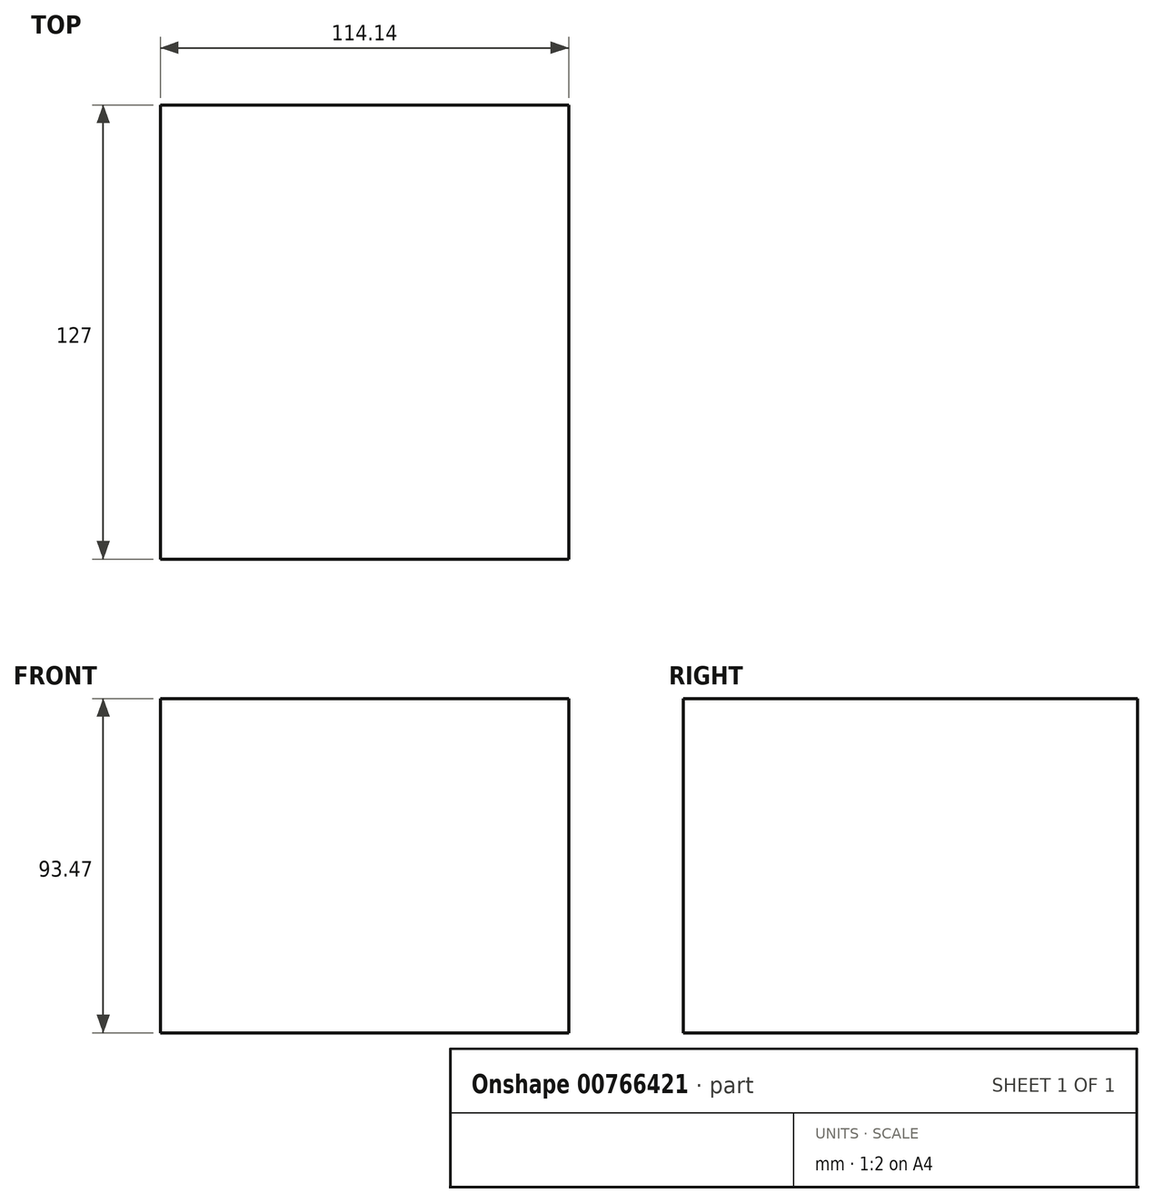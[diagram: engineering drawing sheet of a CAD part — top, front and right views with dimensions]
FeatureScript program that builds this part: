
annotation { "Feature Type Name" : "Feature", "Feature Type Description" : "" }
export const myFeature = defineFeature(function(context is Context, id is Id, definition is map)
    precondition{}
    {
        {
            var Q0;
            Q0=qCreatedBy(makeId("Front.planeOp"),FACE);
            var sketch = newSketch(context, id + "F0", { "sketchPlane" : qUnion([Q0])});
            skLineSegment(sketch, "E0.bottom", {"start": v(-44.65, 36.3) * mm, "end": v(69.49, 36.3) * mm});
            skLineSegment(sketch, "E0.top", {"start": v(-44.65, -57.16) * mm, "end": v(69.49, -57.16) * mm});
            skLineSegment(sketch, "E0.left", {"start": v(-44.65, 36.3) * mm, "end": v(-44.65, -57.16) * mm});
            skLineSegment(sketch, "E0.right", {"start": v(69.49, 36.3) * mm, "end": v(69.49, -57.16) * mm});
            skSolve(sketch);
        }
        {
            var Q0;
            Q0=makeQuery(id+"F0.imprint","IMPRINT",FACE,{"disambiguationData":[TD([[makeQuery(id+"F0.imprint","IMPRINT",EDGE,{"derivedFrom":sQuery(id+"F0.wireOp",EDGE,"E0.bottom")}),-1.0]])]});
            extrude(context, id + "F1", {"entities" : qUnion([Q0]), "depth" : 127 * mm, "offsetDistance" : 25.4 * mm});
        }
    });
